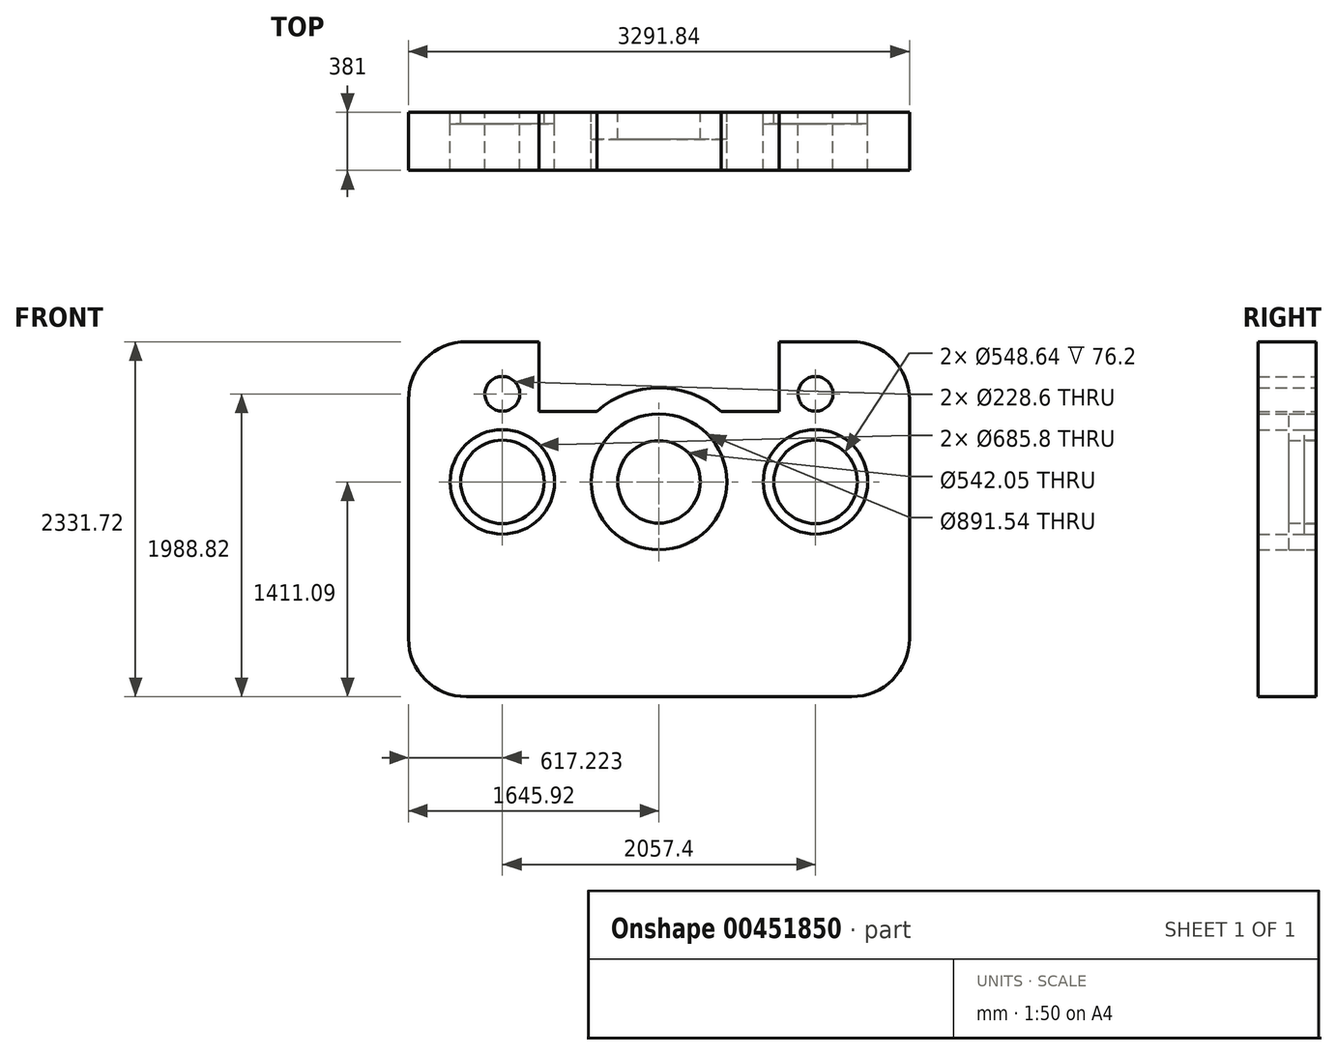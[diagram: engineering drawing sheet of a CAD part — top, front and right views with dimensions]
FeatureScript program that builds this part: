
annotation { "Feature Type Name" : "Feature", "Feature Type Description" : "" }
export const myFeature = defineFeature(function(context is Context, id is Id, definition is map)
    precondition{}
    {
        {
            var Q0;
            Q0=qCreatedBy(makeId("Front.planeOp"),FACE);
            var sketch = newSketch(context, id + "F0", { "sketchPlane" : qUnion([Q0])});
            skArc(sketch, "E0", {"start": v(2191.92, 1100.47) * mm, "mid": v(2080.33, 1369.87) * mm, "end": v(1810.92, 1481.47) * mm});
            skLineSegment(sketch, "E1", {"start": v(1810.92, 1481.47) * mm, "end": v(1334.67, 1481.47) * mm});
            skArc(sketch, "E2", {"start": v(-718.92, 1481.47) * mm, "mid": v(-988.32, 1369.87) * mm, "end": v(-1099.92, 1100.47) * mm});
            skArc(sketch, "E3", {"start": v(-1099.92, -469.25) * mm, "mid": v(-988.32, -738.66) * mm, "end": v(-718.92, -850.25) * mm});
            skLineSegment(sketch, "E4", {"start": v(-1099.92, 1100.47) * mm, "end": v(-1099.92, -469.25) * mm});
            skLineSegment(sketch, "E5", {"start": v(-718.92, -850.25) * mm, "end": v(1810.92, -850.25) * mm});
            skArc(sketch, "E6", {"start": v(1810.92, -850.25) * mm, "mid": v(2080.33, -738.66) * mm, "end": v(2191.92, -469.25) * mm});
            skLineSegment(sketch, "E7", {"start": v(2191.92, -469.25) * mm, "end": v(2191.92, 1100.47) * mm});
            skArc(sketch, "E8", {"start": v(953.67, 1024.27) * mm, "mid": v(546, 1178.06) * mm, "end": v(138.33, 1024.27) * mm});
            skLineSegment(sketch, "E9", {"start": v(-242.67, 1481.47) * mm, "end": v(-242.67, 1024.27) * mm});
            skLineSegment(sketch, "E10", {"start": v(-242.67, 1024.27) * mm, "end": v(138.33, 1024.27) * mm});
            skLineSegment(sketch, "E11", {"start": v(953.67, 1024.27) * mm, "end": v(1334.67, 1024.27) * mm});
            skLineSegment(sketch, "E12", {"start": v(1334.67, 1024.27) * mm, "end": v(1334.67, 1481.47) * mm});
            skLineSegment(sketch, "E13", {"start": v(1810.92, 1481.47) * mm, "end": v(1498.29, 1481.47) * mm});
            skCircle(sketch, "E14", {"center": v(1574.7, 1138.57) * mm, "radius": 114.3 * mm});
            skCircle(sketch, "E15", {"center": v(-482.7, 1138.57) * mm, "radius": 114.3 * mm});
            skLineSegment(sketch, "E16.trimOffspring", {"start": v(-242.67, 1481.47) * mm, "end": v(-718.92, 1481.47) * mm});
            skCircle(sketch, "E17", {"center": v(546, 560.84) * mm, "radius": 445.77 * mm});
            skCircle(sketch, "E18", {"center": v(546, 560.84) * mm, "radius": 271.03 * mm});
            skCircle(sketch, "E19", {"center": v(-482.7, 560.84) * mm, "radius": 342.9 * mm});
            skCircle(sketch, "E20", {"center": v(1574.7, 560.84) * mm, "radius": 342.9 * mm});
            skCircle(sketch, "E21", {"center": v(-482.7, 560.84) * mm, "radius": 274.32 * mm});
            skCircle(sketch, "E22", {"center": v(1574.7, 560.84) * mm, "radius": 274.32 * mm});
            skPoint(sketch, "E23.startSnap0", {"position": v(-242.67, 1252.87) * mm});
            skSolve(sketch);
        }
        {
            var Q0;
            Q0=makeQuery(id+"F0.imprint","IMPRINT",FACE,{"disambiguationData":[TD([[makeQuery(id+"F0.imprint","IMPRINT",EDGE,{"derivedFrom":sQuery(id+"F0.wireOp",EDGE,"E19")}),1.0]])]});
            var Q1;
            Q1=makeQuery(id+"F0.imprint","IMPRINT",FACE,{"disambiguationData":[TD([[makeQuery(id+"F0.imprint","IMPRINT",EDGE,{"derivedFrom":sQuery(id+"F0.wireOp",EDGE,"E20")}),1.0]])]});
            extrude(context, id + "F1", {"entities" : qUnion([Q0, Q1]), "depth" : 76.2 * mm});
        }
        {
            var Q0;
            Q0=makeQuery(id+"F0.imprint","IMPRINT",FACE,{"disambiguationData":[TD([[makeQuery(id+"F0.imprint","IMPRINT",EDGE,{"derivedFrom":sQuery(id+"F0.wireOp",EDGE,"E17")}),1.0]])]});
            extrude(context, id + "F2", {"entities" : qUnion([Q0]), "depth" : 177.8 * mm});
        }
        {
            var Q0;
            Q0=makeQuery(id+"F0.imprint","IMPRINT",FACE,{"disambiguationData":[TD([[makeQuery(id+"F0.imprint","IMPRINT",EDGE,{"derivedFrom":sQuery(id+"F0.wireOp",EDGE,"E0")}),1.0]])]});
            extrude(context, id + "F3", {"entities" : qUnion([Q0]), "depth" : 381 * mm});
        }
    });
